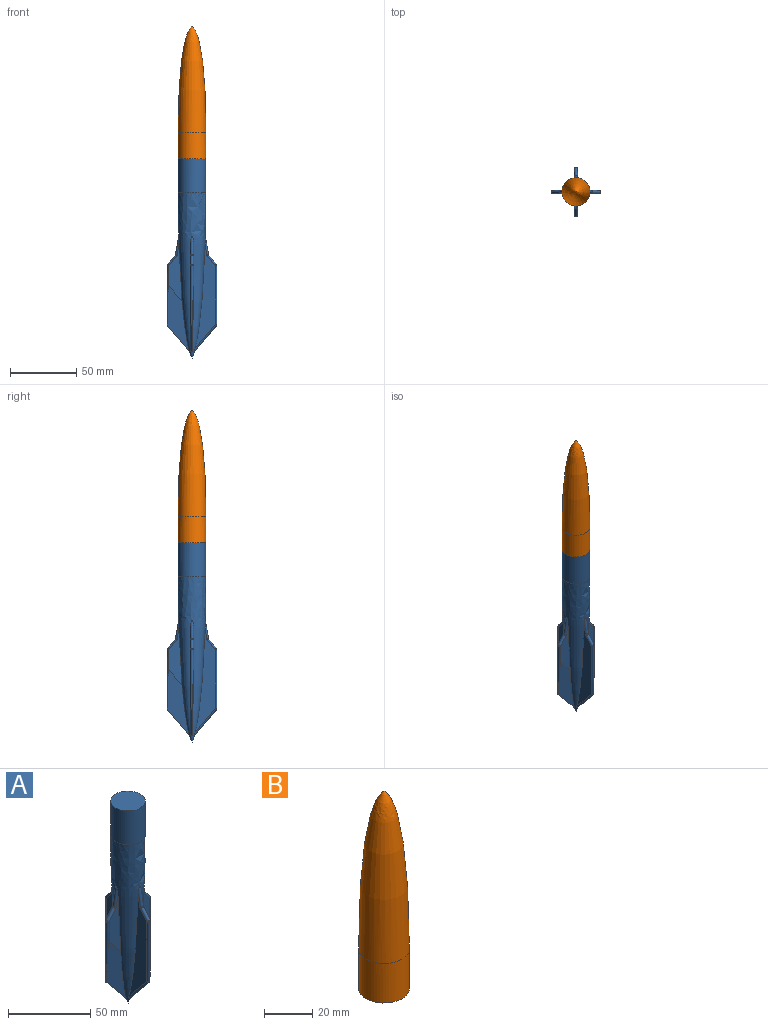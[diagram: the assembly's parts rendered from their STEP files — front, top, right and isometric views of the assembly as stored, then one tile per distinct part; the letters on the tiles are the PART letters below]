
ASSEMBLY  parts=2 mates=1
PART A: 42 faces, bbox 37.5x37.5x145.3 mm
  f0: revolved ~120.27x20.96mm, area 190.7mm2, adj f1,f6,f7,f8,f9,f11
  f1: plane 78.54x15.33mm, normal (0,-1,0), area 582.6mm2, adj f0,f2,f3,f5,f6,f11
  f2: torus R=2.5mm, axis (0,1,0), area 3.5mm2, adj f1,f3,f8,f11
  f3: cylinder r=1.25mm len=7.65mm, axis (-0.64,0,0.77), area 35.1mm2, adj f1,f2,f4,f8
  f4: sphere r=1.25mm, area 2.2mm2, adj f3,f5
  f5: cylinder r=1.25mm len=44.85mm, axis (0,0,1), area 137.9mm2, adj f1,f4,f6,f7,f8
  f6: cylinder r=1.25mm len=20.92mm, axis (-0.64,0,-0.77), area 50mm2, adj f0,f1,f5,f7
  f7: plane 49.78x16.88mm, normal (0.05,1,-0.04), area 409mm2, adj f0,f5,f6,f8
  f8: plane 43.06x10.04mm, normal (0,1,0), area 230.5mm2, adj f0,f2,f3,f5,f7,f11
  f9: cylinder r=10.5mm len=25mm, axis (0,0,-1), area 1649.3mm2, adj f0,f10
  f10: plane 21x21mm, normal (0,0,1), area 346.4mm2, adj f9
  f11: cylinder r=1.25mm len=13.78mm, axis (-0.17,0,0.99), area 42.7mm2, adj f0,f1,f2,f8
  f12: revolved ~86.77x8.5mm, area 190.7mm2, adj f13,f18,f19,f20,f21
  f13: plane 78.54x15.33mm, normal (-1,0,0), area 582.6mm2, adj f12,f14,f15,f17,f18,f21
  f14: torus R=2.5mm, axis (-1,0,0), area 3.5mm2, adj f13,f15,f20,f21
  f15: cylinder r=1.25mm len=7.65mm, axis (0,-0.64,0.77), area 35.1mm2, adj f13,f14,f16,f20
  f16: sphere r=1.25mm, area 2.2mm2, adj f15,f17
  f17: cylinder r=1.25mm len=44.85mm, axis (0,0,1), area 137.9mm2, adj f13,f16,f18,f19,f20
  f18: cylinder r=1.25mm len=20.92mm, axis (0,-0.64,-0.77), area 50mm2, adj f12,f13,f17,f19
  f19: plane 49.78x16.88mm, normal (1,-0.05,0.04), area 409mm2, adj f12,f17,f18,f20
  f20: plane 43.06x10.04mm, normal (1,0,0), area 230.5mm2, adj f12,f14,f15,f17,f19,f21
  f21: cylinder r=1.25mm len=13.78mm, axis (0,-0.17,0.99), area 45.9mm2, adj f12,f13,f14,f20
  f22: revolved ~86.77x8.5mm, area 190.7mm2, adj f23,f28,f29,f30,f31
  f23: cylinder r=1.25mm len=13.78mm, axis (0.17,0,0.99), area 45.9mm2, adj f22,f24,f28,f31
  f24: torus R=2.5mm, axis (0,-1,0), area 3.5mm2, adj f23,f25,f28,f31
  f25: cylinder r=1.25mm len=7.65mm, axis (0.64,0,0.77), area 35.1mm2, adj f24,f26,f28,f31
  f26: sphere r=1.25mm, area 2.2mm2, adj f25,f27
  f27: cylinder r=1.25mm len=44.85mm, axis (0,0,1), area 137.9mm2, adj f26,f28,f29,f30,f31
  f28: plane 78.54x15.33mm, normal (0,-1,0), area 582.6mm2, adj f22,f23,f24,f25,f27,f29
  f29: cylinder r=1.25mm len=20.92mm, axis (0.64,0,-0.77), area 50mm2, adj f22,f27,f28,f30
  f30: plane 49.78x16.88mm, normal (0.05,1,0.04), area 409mm2, adj f22,f27,f29,f31
  f31: plane 43.06x10.04mm, normal (0,1,0), area 230.5mm2, adj f22,f23,f24,f25,f27,f30
  f32: revolved ~86.77x8.5mm, area 190.7mm2, adj f33,f38,f39,f40,f41
  f33: plane 49.78x16.88mm, normal (-1,0.05,0.04), area 409mm2, adj f32,f34,f38,f41
  f34: cylinder r=1.25mm len=44.85mm, axis (0,0,1), area 137.9mm2, adj f33,f35,f38,f40,f41
  f35: sphere r=1.25mm, area 2.2mm2, adj f34,f36
  f36: cylinder r=1.25mm len=7.65mm, axis (0,0.64,0.77), area 35.1mm2, adj f35,f37,f38,f40
  f37: torus R=2.5mm, axis (1,0,0), area 3.5mm2, adj f36,f38,f39,f40
  f38: plane 43.06x10.04mm, normal (-1,0,0), area 230.5mm2, adj f32,f33,f34,f36,f37,f39
  f39: cylinder r=1.25mm len=13.78mm, axis (0,0.17,0.99), area 45.9mm2, adj f32,f37,f38,f40
  f40: plane 78.54x15.33mm, normal (1,0,0), area 582.6mm2, adj f32,f34,f36,f37,f39,f41
  f41: cylinder r=1.25mm len=20.92mm, axis (0,0.64,-0.77), area 50mm2, adj f32,f33,f34,f40
PART B: 3 faces, bbox 21x21x100 mm
  f0: plane 21x21mm, normal (0,0,-1), area 346.4mm2, adj f1
  f1: cylinder r=10.5mm len=21mm, axis (0,0,-1), area 1319.5mm2, adj f0,f2
  f2: revolved ~80x21mm, area 4202.7mm2, adj f1
PLACE A t=(-11.12,21.12,-8.69)mm
PLACE B t=(-11.12,21.12,-8.69)mm
MATE fastened A.f9 <-> B.f1  axis (0,0,1) through (-11.12,21.12,-8.69)mm
